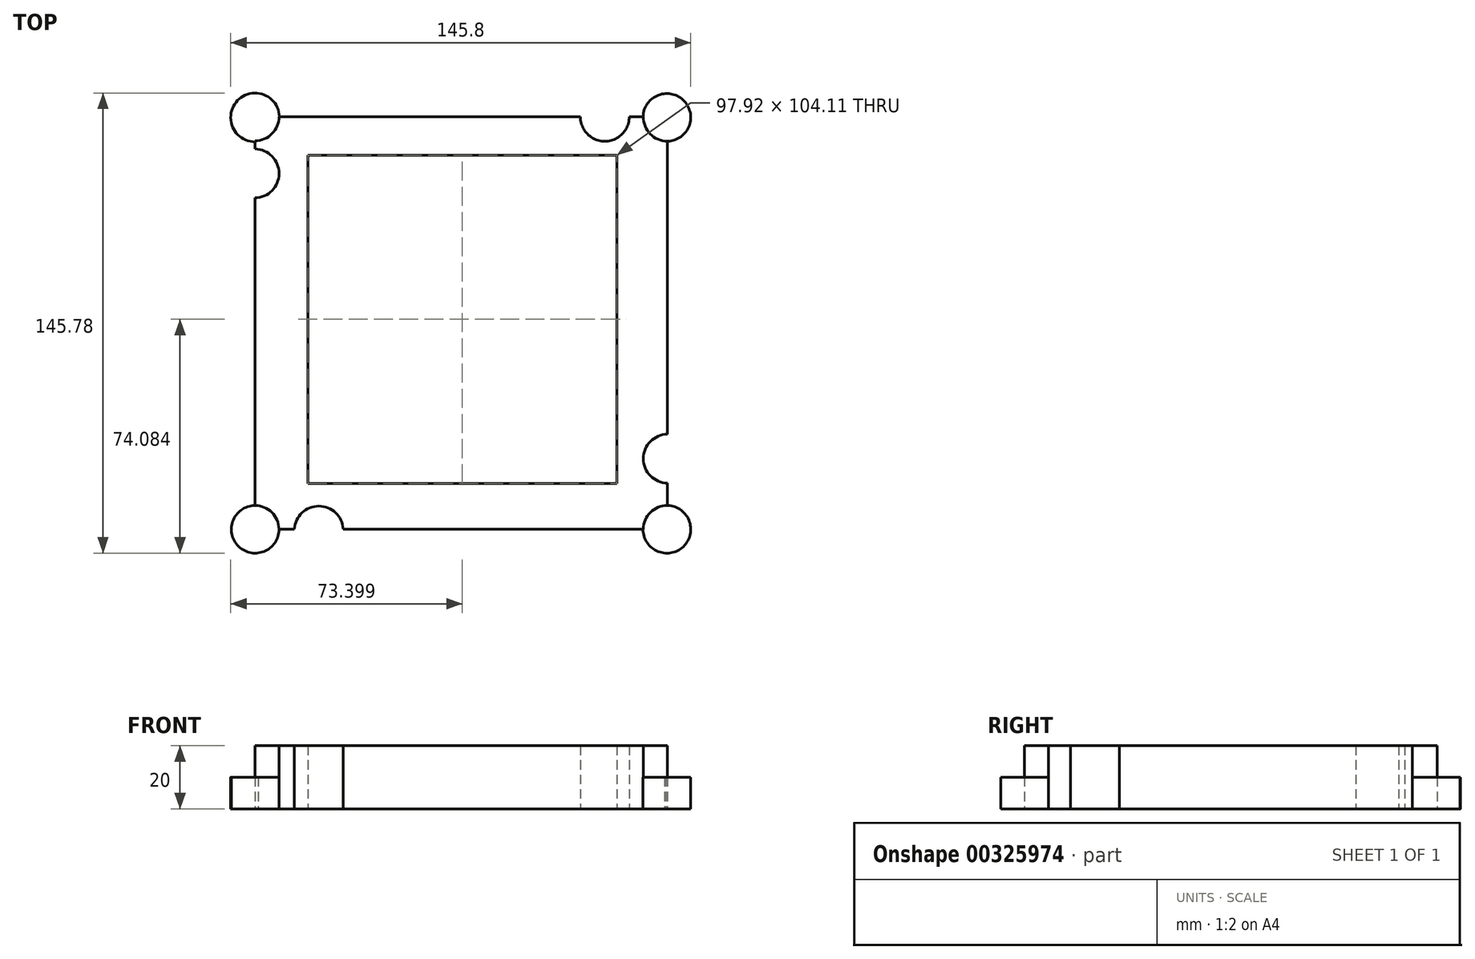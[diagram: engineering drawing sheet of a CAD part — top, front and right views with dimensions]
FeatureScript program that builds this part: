
annotation { "Feature Type Name" : "Feature", "Feature Type Description" : "" }
export const myFeature = defineFeature(function(context is Context, id is Id, definition is map)
    precondition{}
    {
        {
            var Q0;
            Q0=qCreatedBy(makeId("Top.planeOp"),FACE);
            var sketch = newSketch(context, id + "F0", { "sketchPlane" : qUnion([Q0])});
            skLineSegment(sketch, "E0.bottom", {"start": v(-65.35, 65.35) * mm, "end": v(65.35, 65.35) * mm});
            skLineSegment(sketch, "E0.top", {"start": v(-65.35, -65.35) * mm, "end": v(65.35, -65.35) * mm});
            skLineSegment(sketch, "E0.left", {"start": v(-65.35, 65.35) * mm, "end": v(-65.35, -65.35) * mm});
            skLineSegment(sketch, "E0.right", {"start": v(65.35, 65.35) * mm, "end": v(65.35, -65.35) * mm});
            skPoint(sketch, "E0.middle", {"position": v(0, 0) * mm});
            skSolve(sketch);
        }
        {
            var Q0;
            Q0=makeQuery(id+"F0.imprint","IMPRINT",FACE,{"disambiguationData":[TD([[makeQuery(id+"F0.imprint","IMPRINT",EDGE,{"derivedFrom":sQuery(id+"F0.wireOp",EDGE,"E0.bottom")}),-1.0]])]});
            extrude(context, id + "F1", {"entities" : qUnion([Q0]), "depth" : 20 * mm});
        }
        {
            var Q0;
            Q0=qCreatedBy(makeId("Top.planeOp"),FACE);
            var sketch = newSketch(context, id + "F2", { "sketchPlane" : qUnion([Q0])});
            skCircle(sketch, "E1", {"center": v(65.36, -65.56) * mm, "radius": 7.75 * mm});
            skCircle(sketch, "E2", {"center": v(-45.16, -65.79) * mm, "radius": 7.75 * mm});
            skCircle(sketch, "E3", {"center": v(-65.5, -65.56) * mm, "radius": 7.75 * mm});
            skCircle(sketch, "E4", {"center": v(-65.5, 47.37) * mm, "radius": 7.75 * mm});
            skLineSegment(sketch, "E5.bottom", {"start": v(-65.5, 54.96) * mm, "end": v(-73.25, 54.96) * mm});
            skLineSegment(sketch, "E5.top", {"start": v(-65.5, -65.37) * mm, "end": v(-73.25, -65.37) * mm});
            skLineSegment(sketch, "E5.left", {"start": v(-65.5, 54.96) * mm, "end": v(-65.5, -65.37) * mm});
            skLineSegment(sketch, "E5.right", {"start": v(-73.25, 54.96) * mm, "end": v(-73.25, -65.37) * mm});
            skCircle(sketch, "E6", {"center": v(-65.5, 65.41) * mm, "radius": 7.75 * mm});
            skCircle(sketch, "E7", {"center": v(45.48, 65.28) * mm, "radius": 7.73 * mm});
            skCircle(sketch, "E8", {"center": v(65.42, 65.28) * mm, "radius": 7.75 * mm});
            skCircle(sketch, "E9", {"center": v(65.42, -43.01) * mm, "radius": 7.75 * mm});
            skLineSegment(sketch, "E10.bottom", {"start": v(65.42, 65.28) * mm, "end": v(73.15, 65.28) * mm});
            skLineSegment(sketch, "E11.bottom", {"start": v(-65.5, 73.13) * mm, "end": v(53.2, 73.13) * mm});
            skLineSegment(sketch, "E11.top", {"start": v(-65.5, 65.41) * mm, "end": v(53.2, 65.41) * mm});
            skLineSegment(sketch, "E11.left", {"start": v(-65.5, 65.41) * mm, "end": v(-65.5, 73.13) * mm});
            skLineSegment(sketch, "E11.right", {"start": v(53.2, 65.41) * mm, "end": v(53.2, 73.13) * mm});
            skLineSegment(sketch, "E12.bottom", {"start": v(65.42, 65.28) * mm, "end": v(73.27, 65.28) * mm});
            skLineSegment(sketch, "E12.top", {"start": v(65.42, -50.74) * mm, "end": v(73.27, -50.74) * mm});
            skLineSegment(sketch, "E12.left", {"start": v(65.42, 65.28) * mm, "end": v(65.42, -50.74) * mm});
            skLineSegment(sketch, "E12.right", {"start": v(73.27, 65.28) * mm, "end": v(73.27, -50.74) * mm});
            skLineSegment(sketch, "E13.bottom", {"start": v(-52.9, -65.38) * mm, "end": v(65.46, -65.38) * mm});
            skLineSegment(sketch, "E13.top", {"start": v(-52.9, -73.3) * mm, "end": v(65.46, -73.3) * mm});
            skLineSegment(sketch, "E13.left", {"start": v(-52.9, -65.38) * mm, "end": v(-52.9, -73.3) * mm});
            skLineSegment(sketch, "E13.right", {"start": v(65.46, -65.38) * mm, "end": v(65.46, -73.3) * mm});
            skSolve(sketch);
        }
        {
            var Q0;
            Q0 = qSketchRegion(id + "F2", true);
            extrude(context, id + "F3", {"entities" : qUnion([Q0]), "operationType" : NewBodyOperationType.REMOVE, "depth" : 20 * mm});
        }
        {
            var Q0;
            Q0=qCreatedBy(makeId("Top.planeOp"),FACE);
            var sketch = newSketch(context, id + "F4", { "sketchPlane" : qUnion([Q0])});
            skLineSegment(sketch, "E14.bottom", {"start": v(-48.65, 53.19) * mm, "end": v(49.27, 53.19) * mm});
            skLineSegment(sketch, "E14.top", {"start": v(-48.65, -50.92) * mm, "end": v(49.27, -50.92) * mm});
            skLineSegment(sketch, "E14.left", {"start": v(-48.65, 53.19) * mm, "end": v(-48.65, -50.92) * mm});
            skLineSegment(sketch, "E14.right", {"start": v(49.27, 53.19) * mm, "end": v(49.27, -50.92) * mm});
            skSolve(sketch);
        }
        {
            var Q0;
            Q0 = qSketchRegion(id + "F4", true);
            extrude(context, id + "F5", {"entities" : qUnion([Q0]), "operationType" : NewBodyOperationType.REMOVE, "depth" : 25 * mm});
        }
        {
            var Q0;
            Q0=qCreatedBy(makeId("Top.planeOp"),FACE);
            var sketch = newSketch(context, id + "F6", { "sketchPlane" : qUnion([Q0])});
            skCircle(sketch, "E15", {"center": v(-65.37, 65.11) * mm, "radius": 7.72 * mm});
            skPoint(sketch, "E15.first.point", {"position": v(-65.39, 57.4) * mm});
            skPoint(sketch, "E15.second.point", {"position": v(-57.66, 65.4) * mm});
            skPoint(sketch, "E15.third.point", {"position": v(-69.24, 71.78) * mm});
            skCircle(sketch, "E16", {"center": v(65.15, 65.11) * mm, "radius": 7.56 * mm});
            skCircle(sketch, "E17", {"center": v(65.15, -65.4) * mm, "radius": 7.56 * mm});
            skCircle(sketch, "E18", {"center": v(-65.32, -65.4) * mm, "radius": 7.56 * mm});
            skSolve(sketch);
        }
        {
            var Q0;
            Q0=makeQuery(id+"F6.imprint","IMPRINT",FACE,{"disambiguationData":[TD([[makeQuery(id+"F6.imprint","IMPRINT",EDGE,{"derivedFrom":sQuery(id+"F6.wireOp",EDGE,"E18")}),1.0]])]});
            var Q1;
            Q1=makeQuery(id+"F6.imprint","IMPRINT",FACE,{"disambiguationData":[TD([[makeQuery(id+"F6.imprint","IMPRINT",EDGE,{"derivedFrom":sQuery(id+"F6.wireOp",EDGE,"E17")}),1.0]])]});
            var Q2;
            Q2=makeQuery(id+"F6.imprint","IMPRINT",FACE,{"disambiguationData":[TD([[makeQuery(id+"F6.imprint","IMPRINT",EDGE,{"derivedFrom":sQuery(id+"F6.wireOp",EDGE,"E15")}),1.0]])]});
            var Q3;
            Q3=makeQuery(id+"F6.imprint","IMPRINT",FACE,{"disambiguationData":[TD([[makeQuery(id+"F6.imprint","IMPRINT",EDGE,{"derivedFrom":sQuery(id+"F6.wireOp",EDGE,"E16")}),1.0]])]});
            var Q4;
            Q4=sQuery(id+"F6.wireOp",EDGE,"E18");
            var Q5;
            Q5=sQuery(id+"F6.wireOp",EDGE,"E16");
            var Q6;
            Q6=sQuery(id+"F6.wireOp",EDGE,"E15");
            var Q7;
            Q7=sQuery(id+"F6.wireOp",EDGE,"E17");
            extrude(context, id + "F7", {"entities" : qUnion([Q0, Q1, Q2, Q3]), "operationType" : NewBodyOperationType.ADD, "surfaceEntities" : qUnion([Q4, Q5, Q6, Q7]), "depth" : 10 * mm});
        }
    });
